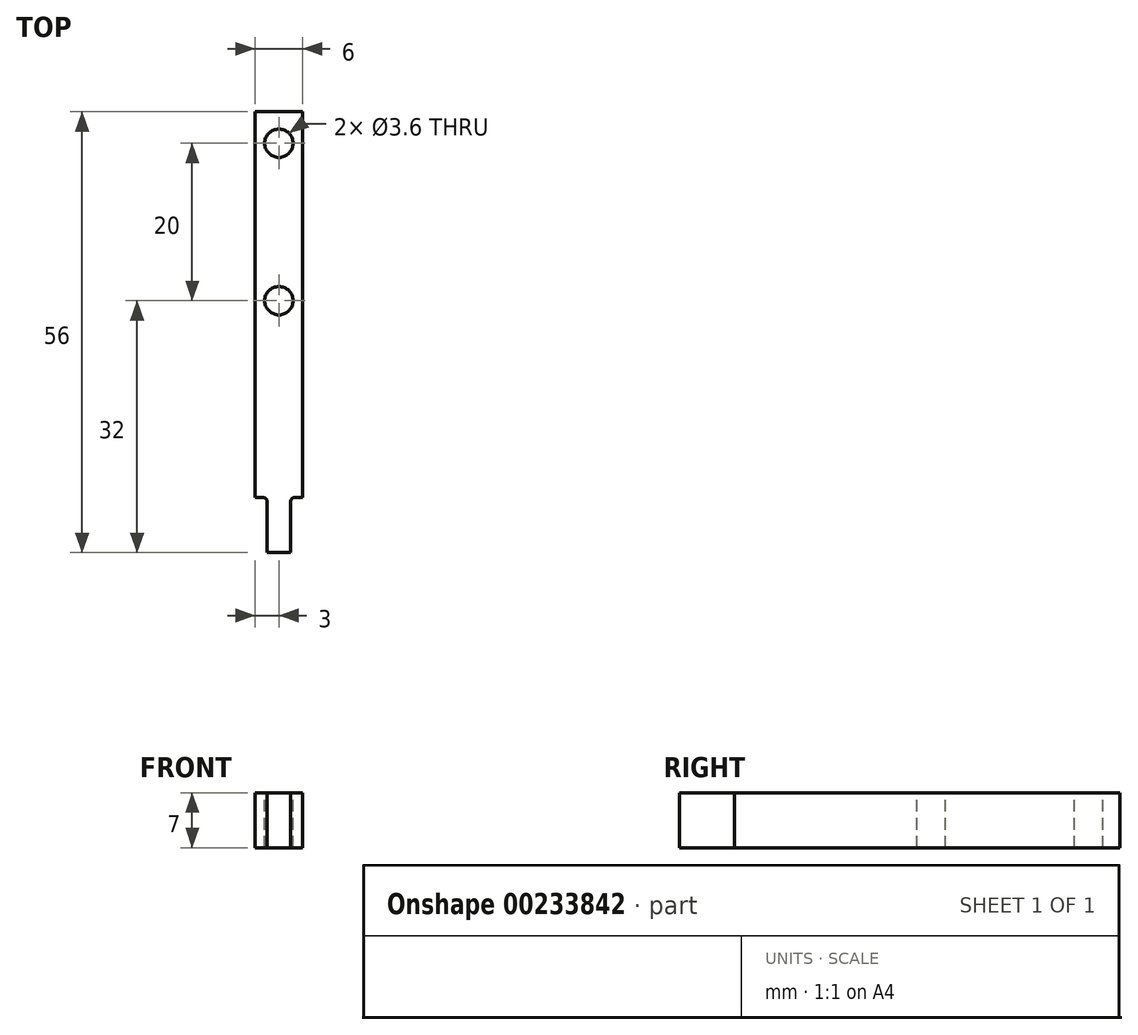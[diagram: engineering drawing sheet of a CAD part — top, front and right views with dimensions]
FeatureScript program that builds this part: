
annotation { "Feature Type Name" : "Feature", "Feature Type Description" : "" }
export const myFeature = defineFeature(function(context is Context, id is Id, definition is map)
    precondition{}
    {
        {
            var Q0;
            Q0=qCreatedBy(makeId("Top.planeOp"),FACE);
            var sketch = newSketch(context, id + "F0", { "sketchPlane" : qUnion([Q0])});
            skLineSegment(sketch, "E0.bottom", {"start": v(0, 0) * mm, "end": v(6, 0) * mm});
            skLineSegment(sketch, "E0.top", {"start": v(0, 56) * mm, "end": v(6, 56) * mm});
            skLineSegment(sketch, "E0.left", {"start": v(0, 0) * mm, "end": v(0, 56) * mm});
            skLineSegment(sketch, "E0.right", {"start": v(6, 0) * mm, "end": v(6, 56) * mm});
            skSolve(sketch);
        }
        {
            var Q0;
            Q0 = qSketchRegion(id + "F0", true);
            extrude(context, id + "F1", {"entities" : qUnion([Q0]), "depth" : 7 * mm});
        }
        {
            var Q0;
            Q0=makeQuery(id+"F1.opExtrude","CAP_FACE",FACE,{"disambiguationData":[OSD([sQuery(id+"F0.wireOp",EDGE,"E0.bottom"),sQuery(id+"F0.wireOp",EDGE,"E0.top"),sQuery(id+"F0.wireOp",EDGE,"E0.left"),sQuery(id+"F0.wireOp",EDGE,"E0.right")])],"isStart":false});
            var sketch = newSketch(context, id + "F2", { "sketchPlane" : qUnion([Q0])});
            skLineSegment(sketch, "E1", {"start": v(3, 56) * mm, "end": v(3, 0) * mm, "construction": true});
            skCircle(sketch, "E2", {"center": v(3, 52) * mm, "radius": 1.8 * mm});
            skCircle(sketch, "E3", {"center": v(3, 32) * mm, "radius": 1.8 * mm});
            skSolve(sketch);
        }
        {
            var Q0;
            Q0 = qSketchRegion(id + "F2", true);
            extrude(context, id + "F3", {"entities" : qUnion([Q0]), "operationType" : NewBodyOperationType.REMOVE, "endBound" : BoundingType.THROUGH_ALL, "oppositeDirection" : true, "depth" : 25 * mm});
        }
        {
            var Q0;
            Q0=makeQuery(id+"F1.opExtrude","CAP_FACE",FACE,{"disambiguationData":[OSD([sQuery(id+"F0.wireOp",EDGE,"E0.bottom"),sQuery(id+"F0.wireOp",EDGE,"E0.top"),sQuery(id+"F0.wireOp",EDGE,"E0.left"),sQuery(id+"F0.wireOp",EDGE,"E0.right")])],"isStart":false});
            var sketch = newSketch(context, id + "F4", { "sketchPlane" : qUnion([Q0])});
            skLineSegment(sketch, "E4.1", {"start": v(0, 0) * mm, "end": v(1.5, 0) * mm});
            skLineSegment(sketch, "E4.2", {"start": v(6, 0) * mm, "end": v(6, 7) * mm});
            skLineSegment(sketch, "E5", {"start": v(1.5, 0) * mm, "end": v(1.5, 7) * mm});
            skLineSegment(sketch, "E6", {"start": v(4.5, 0) * mm, "end": v(4.5, 7) * mm});
            skLineSegment(sketch, "E7", {"start": v(1.5, 7) * mm, "end": v(0, 7) * mm});
            skLineSegment(sketch, "E8", {"start": v(4.5, 7) * mm, "end": v(6, 7) * mm});
            skPoint(sketch, "E9.orphan", {"position": v(6, 56) * mm});
            skPoint(sketch, "E10.orphan", {"position": v(0, 56) * mm});
            skLineSegment(sketch, "E11.trimOffspring", {"start": v(4.5, 0) * mm, "end": v(6, 0) * mm});
            skLineSegment(sketch, "E12", {"start": v(0, 7) * mm, "end": v(0, 0) * mm});
            skSolve(sketch);
        }
        {
            var Q0;
            Q0 = qSketchRegion(id + "F4", true);
            extrude(context, id + "F5", {"entities" : qUnion([Q0]), "operationType" : NewBodyOperationType.REMOVE, "endBound" : BoundingType.THROUGH_ALL, "oppositeDirection" : true, "depth" : 25 * mm});
        }
        {
            var Q0;
            Q0=makeQuery(id+"F5.boolean.opBoolean","COPY",EDGE,{"derivedFrom":makeQuery(id+"F5.opExtrude","SWEPT_EDGE",EDGE,{"disambiguationData":[OSD([sQuery(id+"F0.wireOp",EDGE,"E0.right"),sQuery(id+"F4.wireOp",EDGE,"E4.2"),sQuery(id+"F4.wireOp",EDGE,"E8")])]})});
            var Q1;
            Q1=makeQuery(id+"F5.boolean.opBoolean","COPY",EDGE,{"derivedFrom":makeQuery(id+"F5.opExtrude","SWEPT_EDGE",EDGE,{"disambiguationData":[OSD([sQuery(id+"F0.wireOp",EDGE,"E0.left"),sQuery(id+"F4.wireOp",EDGE,"E7"),sQuery(id+"F4.wireOp",EDGE,"E12")])]})});
            var Q2;
            Q2=makeQuery(id+"F5.boolean.opBoolean","COPY",EDGE,{"derivedFrom":makeQuery(id+"F5.opExtrude","SWEPT_EDGE",EDGE,{"disambiguationData":[OSD([sQuery(id+"F4.wireOp",EDGE,"E6"),sQuery(id+"F4.wireOp",EDGE,"E8")])]})});
            var Q3;
            Q3=makeQuery(id+"F5.boolean.opBoolean","COPY",EDGE,{"derivedFrom":makeQuery(id+"F5.opExtrude","SWEPT_EDGE",EDGE,{"disambiguationData":[OSD([sQuery(id+"F4.wireOp",EDGE,"E5"),sQuery(id+"F4.wireOp",EDGE,"E7")])]})});
            fillet(context, id + "F6", {"entities" : qUnion([Q0, Q1, Q2, Q3]), "radius" : .5 * mm, "tangentPropagation" : true, "allowEdgeOverflow" : false});
        }
    });
